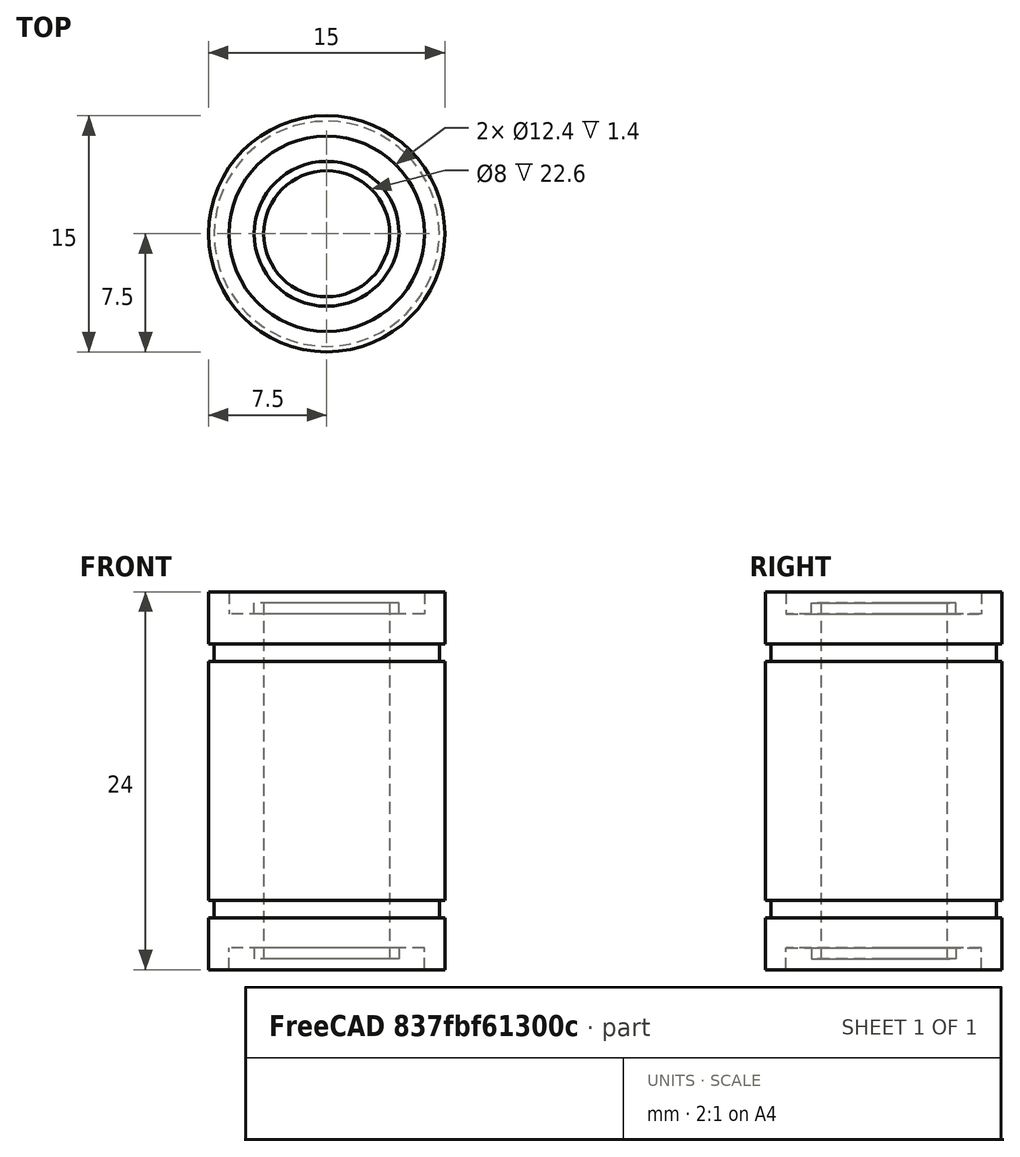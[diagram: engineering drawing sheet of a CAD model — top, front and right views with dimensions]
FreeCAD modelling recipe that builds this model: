
FCSTD DOCUMENT  (FreeCAD 0.14R3702 (Git))
Label: LM8uu
License: CC-BY 3.0
LicenseURL: http://creativecommons.org/licenses/by/3.0/
objects: Sketcher::SketchObject×1, PartDesign::Revolution×1, Part::Feature×1
note: 4 computed .brp shape members not serialized (recipe doc carries the construction recipe); baked Part::Feature solids carry a one-line shape summary decoded from their .brp

FEATURE [Sketcher::SketchObject] Sketch  label="lm8uu-cross-section"
  Placement = pos=(0,0,0) rot=(-1,0,0;4.71239rad)
  sketch-geometry (20):
    g0: LineSegment StartX=7.5 StartY=-12 StartZ=0 EndX=7.5 EndY=-8.7 EndZ=0
    g1: LineSegment StartX=7.5 StartY=7.6 StartZ=0 EndX=7.15 EndY=7.6 EndZ=0
    g2: LineSegment StartX=7.15 StartY=7.6 StartZ=0 EndX=7.15 EndY=8.7 EndZ=0
    g3: LineSegment StartX=7.15 StartY=8.7 StartZ=0 EndX=7.5 EndY=8.7 EndZ=0
    g4: LineSegment StartX=7.5 StartY=8.7 StartZ=0 EndX=7.5 EndY=12 EndZ=0
    g5: LineSegment StartX=7.5 StartY=12 StartZ=0 EndX=6.2 EndY=12 EndZ=0
    g6: LineSegment StartX=6.2 StartY=12 StartZ=0 EndX=6.2 EndY=10.6 EndZ=0
    g7: LineSegment StartX=6.2 StartY=10.6 StartZ=0 EndX=4.6 EndY=10.6 EndZ=0
    g8: LineSegment StartX=4.6 StartY=10.6 StartZ=0 EndX=4.6 EndY=11.3 EndZ=0
    g9: LineSegment StartX=4.6 StartY=11.3 StartZ=0 EndX=4 EndY=11.3 EndZ=0
    g10: LineSegment StartX=4 StartY=11.3 StartZ=0 EndX=4 EndY=-11.3 EndZ=0
    g11: LineSegment StartX=7.5 StartY=-7.6 StartZ=0 EndX=7.15 EndY=-7.6 EndZ=0
    g12: LineSegment StartX=7.15 StartY=-8.7 StartZ=0 EndX=7.5 EndY=-8.7 EndZ=0
    g13: LineSegment StartX=7.5 StartY=-7.6 StartZ=0 EndX=7.5 EndY=7.6 EndZ=0
    g14: LineSegment StartX=7.15 StartY=-7.6 StartZ=0 EndX=7.15 EndY=-8.7 EndZ=0
    g15: LineSegment StartX=7.5 StartY=-12 StartZ=0 EndX=6.2 EndY=-12 EndZ=0
    g16: LineSegment StartX=6.2 StartY=-12 StartZ=0 EndX=6.2 EndY=-10.6 EndZ=0
    g17: LineSegment StartX=6.2 StartY=-10.6 StartZ=0 EndX=4.6 EndY=-10.6 EndZ=0
    g18: LineSegment StartX=4.6 StartY=-10.6 StartZ=0 EndX=4.6 EndY=-11.3 EndZ=0
    g19: LineSegment StartX=4.6 StartY=-11.3 StartZ=0 EndX=4 EndY=-11.3 EndZ=0
  constraints (58):
    c: Coincident(g13,g1)
    c: Coincident(g1,g2)
    c: Vertical(g2)
    c: Coincident(g2,g3)
    c: Coincident(g3,g4)
    c: Vertical(g4)
    c: Coincident(g4,g5)
    c: Coincident(g5,g6)
    c: Vertical(g6)
    c: Coincident(g6,g7)
    c: Horizontal(g7)
    c: Coincident(g7,g8)
    c: Vertical(g8)
    c: Coincident(g8,g9)
    c: Horizontal(g9)
    c: Coincident(g9,g10)
    c: Vertical(g10)
    c: Horizontal(g1)
    c: Horizontal(g5)
    c: Horizontal(g3)
    c: PointOnObject(g3,g0)
    c: Symmetric(g0,g4,g-1)
    c: DistanceY(g4,g0) = -24
    c: DistanceY(g2) = 1.1
    c: DistanceX(g3) = 0.35
    c: DistanceX(g-1,g4) = 7.5
    c: DistanceX(g-1,g9) = 4
    c: DistanceX(g5) = -1.3
    c: DistanceX(g9) = -0.6
    c: DistanceY(g6) = -1.4
    c: DistanceY(g8) = 0.7
    c: Horizontal(g11)
    c: Horizontal(g12)
    c: Coincident(g13,g11)
    c: Tangent(g0,g13)
    c: Coincident(g12,g0)
    c: PointOnObject(g14,g11)
    c: Coincident(g14,g12)
    c: Vertical(g14)
    c: Symmetric(g1,g11,g-1)
    c: DistanceY(g13) = 15.2
    c: Equal(g14,g2)
    c: Coincident(g0,g15)
    c: Horizontal(g15)
    c: Coincident(g15,g16)
    c: Vertical(g16)
    c: Coincident(g16,g17)
    c: Horizontal(g17)
    c: Coincident(g17,g18)
    c: Vertical(g18)
    c: Coincident(g18,g19)
    c: Horizontal(g19)
    c: Coincident(g10,g19)
    c: Symmetric(g10,g9,g-1)
    c: Symmetric(g16,g6,g-1)
    c: Symmetric(g17,g7,g-1)
    c: Coincident(g14,g11)
    c: PointOnObject(g11,g2)
FEATURE [PartDesign::Revolution] Revolution  label="LM8uu"
  Angle = 360
  Axis = (0,0,1)
  Base = (0,0,0)
  Placement = pos=(0,0,0) rot=(-1,0,0;4.71239rad)
  ReferenceAxis = -> Sketch [V_Axis]
  Reversed = true
  Sketch = -> Sketch
FEATURE [Part::Feature] Revolution001  label="LM8uu001"
  Placement = pos=(0,0,0) rot=(1,0,0;1.5708rad)
  shape: bbox 15 x 15 x 24 mm, 20 faces (baked)
